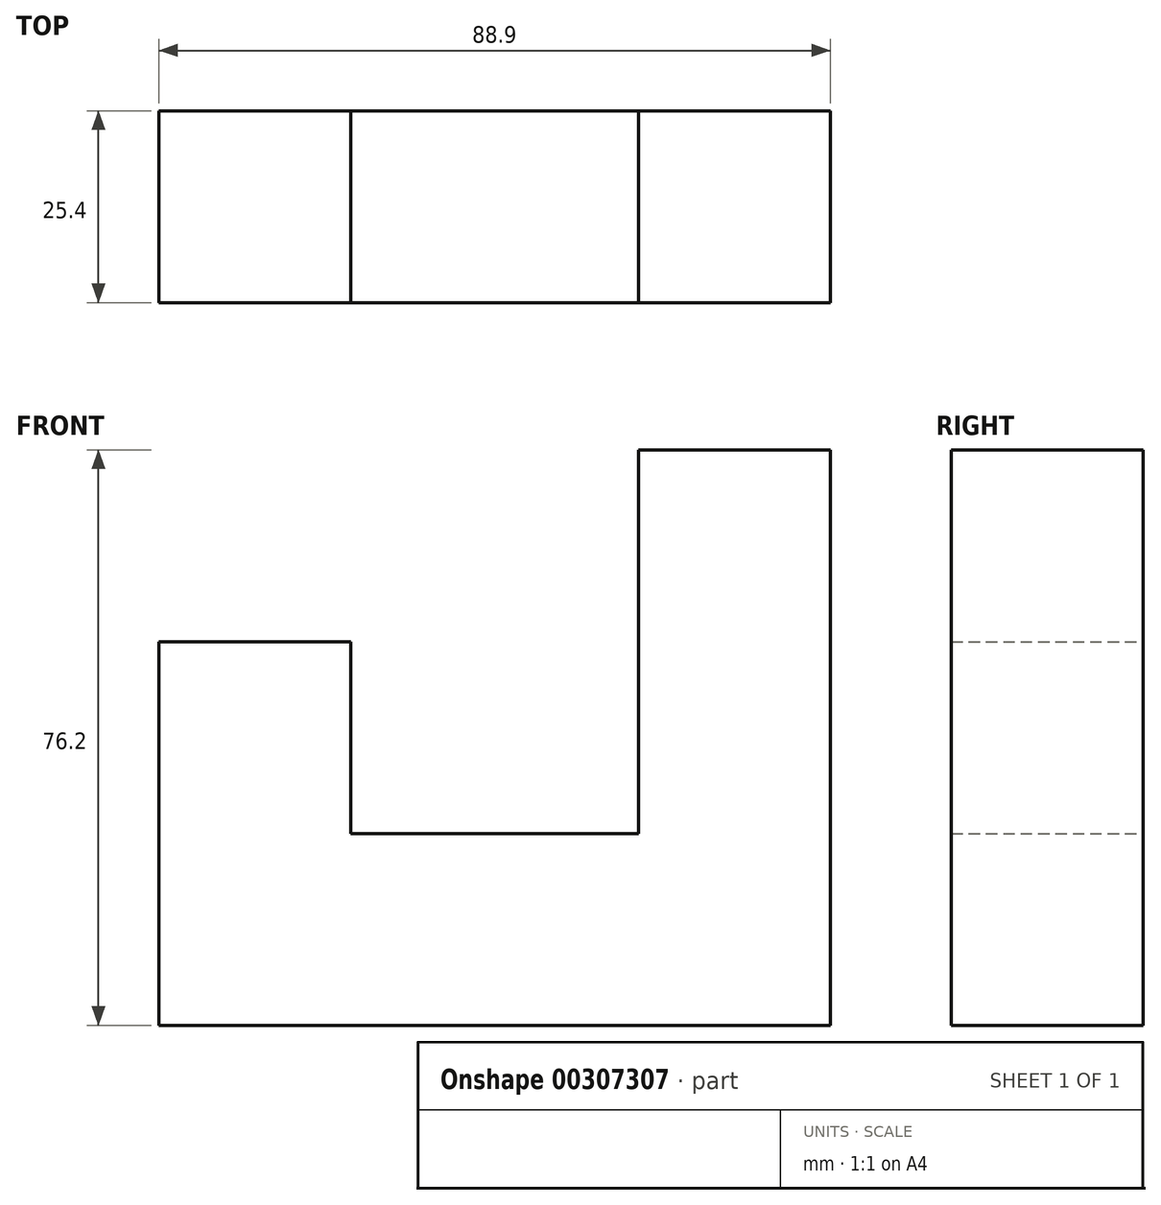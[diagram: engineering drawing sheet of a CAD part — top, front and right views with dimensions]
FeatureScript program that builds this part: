
annotation { "Feature Type Name" : "Feature", "Feature Type Description" : "" }
export const myFeature = defineFeature(function(context is Context, id is Id, definition is map)
    precondition{}
    {
        {
            var Q0;
            Q0=qCreatedBy(makeId("Front.planeOp"),FACE);
            var sketch = newSketch(context, id + "F0", { "sketchPlane" : qUnion([Q0])});
            skLineSegment(sketch, "E0", {"start": v(-45.16, 11.55) * mm, "end": v(-45.16, -39.25) * mm});
            skLineSegment(sketch, "E1", {"start": v(-45.16, -39.25) * mm, "end": v(43.74, -39.25) * mm});
            skLineSegment(sketch, "E2", {"start": v(43.74, -39.25) * mm, "end": v(43.74, 36.95) * mm});
            skLineSegment(sketch, "E3", {"start": v(43.74, 36.95) * mm, "end": v(18.34, 36.95) * mm});
            skLineSegment(sketch, "E4", {"start": v(18.34, 36.95) * mm, "end": v(18.34, -13.85) * mm});
            skLineSegment(sketch, "E5", {"start": v(18.34, -13.85) * mm, "end": v(-19.76, -13.85) * mm});
            skLineSegment(sketch, "E6", {"start": v(-19.76, -13.85) * mm, "end": v(-19.76, 11.55) * mm});
            skLineSegment(sketch, "E7", {"start": v(-19.76, 11.55) * mm, "end": v(-45.16, 11.55) * mm});
            skSolve(sketch);
        }
        {
            var Q0;
            Q0=makeQuery(id+"F0.imprint","IMPRINT",FACE,{"disambiguationData":[TD([[makeQuery(id+"F0.imprint","IMPRINT",EDGE,{"derivedFrom":sQuery(id+"F0.wireOp",EDGE,"E0")}),1.0]])]});
            extrude(context, id + "F1", {"entities" : qUnion([Q0]), "depth" : 25.4 * mm});
        }
    });
